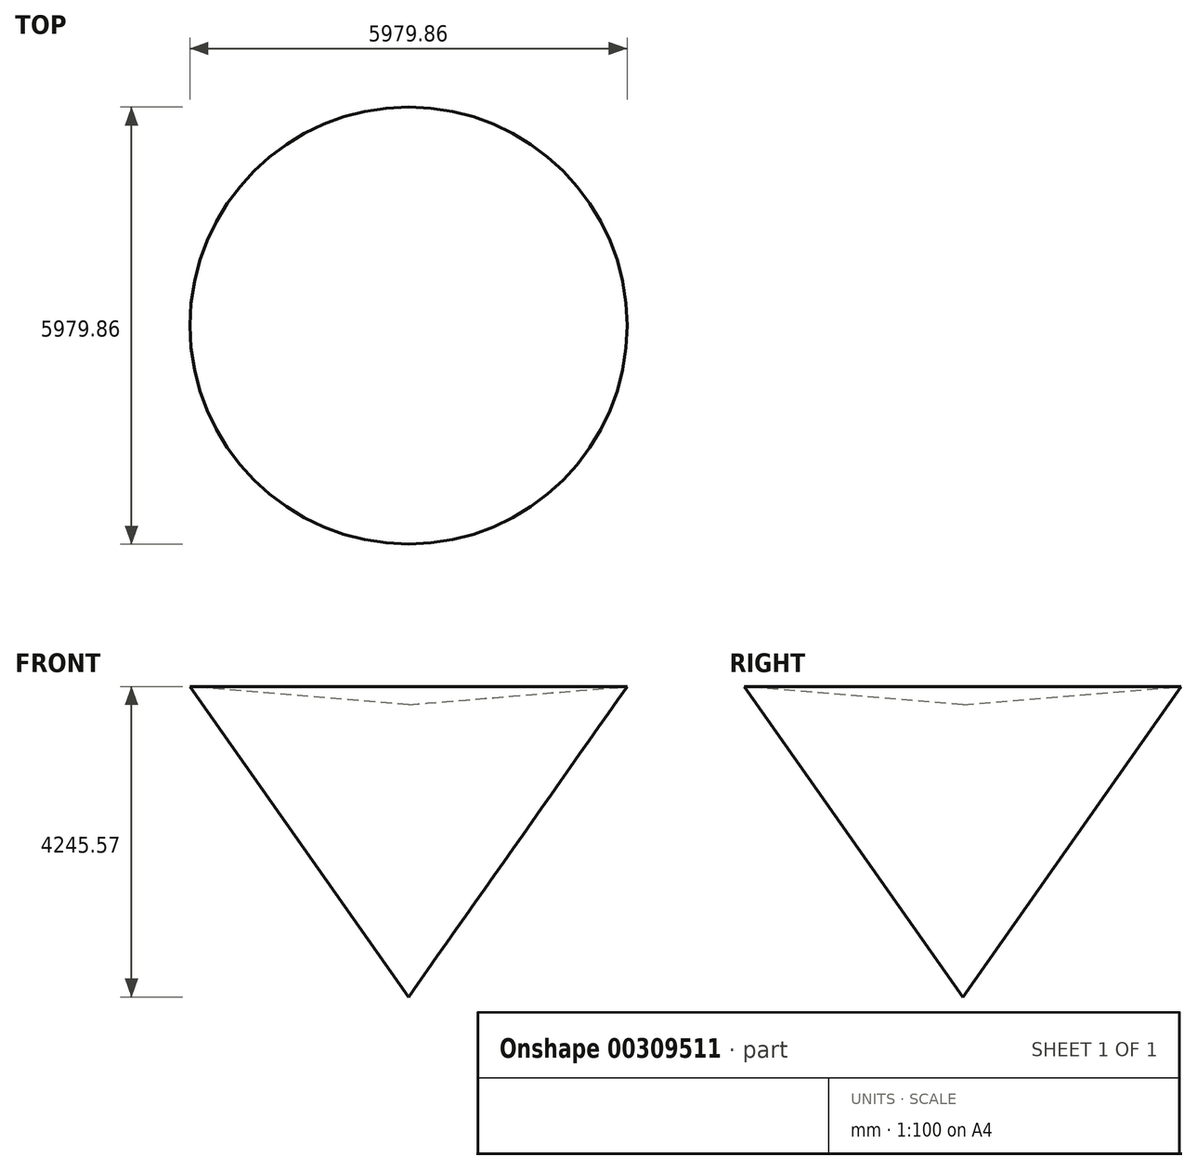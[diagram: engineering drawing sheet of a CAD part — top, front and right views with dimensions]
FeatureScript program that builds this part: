
annotation { "Feature Type Name" : "Feature", "Feature Type Description" : "" }
export const myFeature = defineFeature(function(context is Context, id is Id, definition is map)
    precondition{}
    {
        {
            var Q0;
            Q0=qCreatedBy(makeId("Front.planeOp"),FACE);
            var sketch = newSketch(context, id + "F0", { "sketchPlane" : qUnion([Q0])});
            skLineSegment(sketch, "E0", {"start": v(0, 4137.97) * mm, "end": v(0, 137.97) * mm});
            skLineSegment(sketch, "E1", {"start": v(0, 4137.97) * mm, "end": v(2989.93, 4383.54) * mm});
            skLineSegment(sketch, "E2", {"start": v(0, 137.97) * mm, "end": v(2989.93, 4383.54) * mm});
            skLineSegment(sketch, "E3", {"start": v(0, 45.32) * mm, "end": v(0, -60.39) * mm, "construction": true});
            skSolve(sketch);
        }
        {
            var Q0;
            Q0=makeQuery(id+"F0.imprint","IMPRINT",FACE,{"disambiguationData":[TD([[makeQuery(id+"F0.imprint","IMPRINT",EDGE,{"derivedFrom":sQuery(id+"F0.wireOp",EDGE,"E0")}),1.0]])]});
            var Q1;
            Q1=sQuery(id+"F0.wireOp",EDGE,"E3");
            revolve(context, id + "F1", {"entities" : qUnion([Q0]), "axis" : qUnion([Q1]), "revolveType" : RevolveType.FULL});
        }
    });
